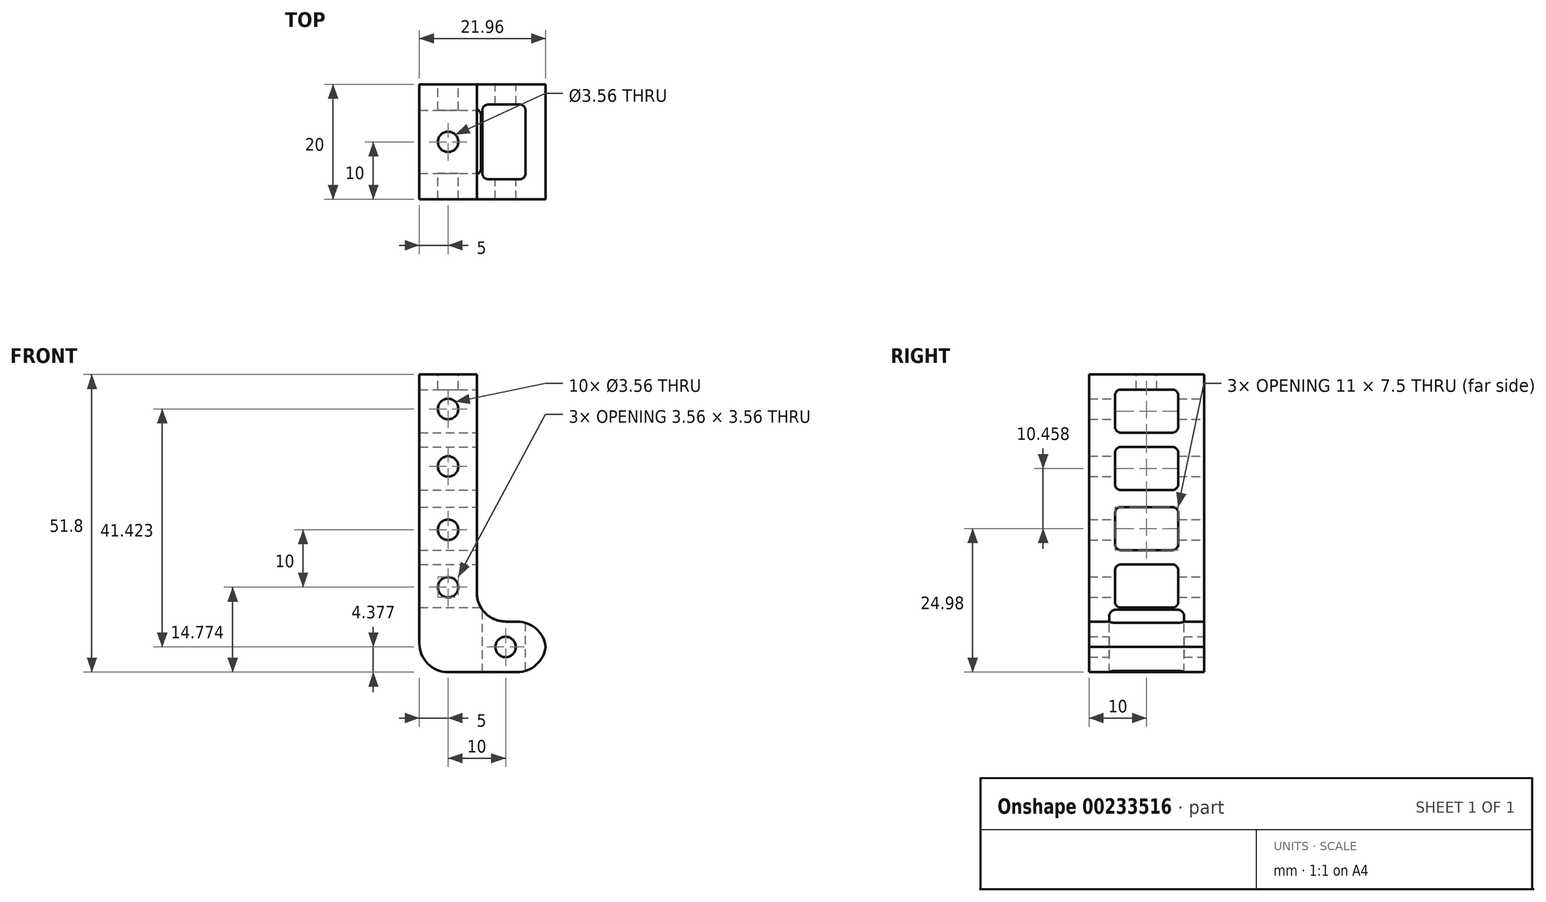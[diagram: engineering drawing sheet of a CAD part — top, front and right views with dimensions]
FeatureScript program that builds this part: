
annotation { "Feature Type Name" : "Feature", "Feature Type Description" : "" }
export const myFeature = defineFeature(function(context is Context, id is Id, definition is map)
    precondition{}
    {
        {
            var Q0;
            Q0=qCreatedBy(makeId("Front.planeOp"),FACE);
            var sketch = newSketch(context, id + "F0", { "sketchPlane" : qUnion([Q0])});
            skLineSegment(sketch, "E0.top", {"start": v(0, 43) * mm, "end": v(10, 43) * mm});
            skLineSegment(sketch, "E0.left", {"start": v(0, 0) * mm, "end": v(0, 43) * mm});
            skLineSegment(sketch, "E0.right", {"start": v(10, 5) * mm, "end": v(10, 43) * mm});
            skCircle(sketch, "E1", {"center": v(5, 15.97) * mm, "radius": 1.78 * mm});
            skCircle(sketch, "E2", {"center": v(5, 5.97) * mm, "radius": 1.78 * mm});
            skCircle(sketch, "E3", {"center": v(15, -4.42) * mm, "radius": 1.78 * mm});
            skLineSegment(sketch, "E4.bottom", {"start": v(15, 0) * mm, "end": v(17, 0) * mm});
            skLineSegment(sketch, "E4.top", {"start": v(5, -8.8) * mm, "end": v(17, -8.8) * mm});
            skLineSegment(sketch, "E4.left", {"start": v(0, 0) * mm, "end": v(0, -3.8) * mm});
            skLineSegment(sketch, "E4.right", {"start": v(22, -3.8) * mm, "end": v(22, -5) * mm});
            skPoint(sketch, "E5.visualSharp", {"position": v(10, 0) * mm});
            skArc(sketch, "E5.filletArc", {"start": v(10, 5) * mm, "mid": v(11.46, 1.46) * mm, "end": v(15, 0) * mm});
            skPoint(sketch, "E6.visualSharp", {"position": v(0, -8.8) * mm});
            skArc(sketch, "E6.filletArc", {"start": v(0, -3.8) * mm, "mid": v(1.46, -7.33) * mm, "end": v(5, -8.8) * mm});
            skPoint(sketch, "E7.visualSharp", {"position": v(22, -8.8) * mm});
            skArc(sketch, "E7.filletArc", {"start": v(17, -8.8) * mm, "mid": v(20.54, -7.33) * mm, "end": v(22, -3.8) * mm});
            skPoint(sketch, "E8.visualSharp", {"position": v(22, 0) * mm});
            skArc(sketch, "E8.filletArc", {"start": v(22, -5) * mm, "mid": v(20.54, -1.46) * mm, "end": v(17, 0) * mm});
            skCircle(sketch, "E9", {"center": v(5, 27) * mm, "radius": 1.78 * mm});
            skCircle(sketch, "E10.0.1.0", {"center": v(5, 37) * mm, "radius": 1.78 * mm});
            skLineSegment(sketch, "E10.direction1", {"start": v(5, 27) * mm, "end": v(30, 27) * mm, "construction": true});
            skLineSegment(sketch, "E10.direction2", {"start": v(5, 27) * mm, "end": v(5, 37) * mm, "construction": true});
            skSolve(sketch);
        }
        {
            var Q0;
            Q0 = qSketchRegion(id + "F0", true);
            extrude(context, id + "F1", {"entities" : qUnion([Q0]), "depth" : 20 * mm});
        }
        {
            var Q0;
            Q0=makeQuery(id+"F1.opExtrude","SWEPT_FACE",FACE,{"disambiguationData":[OSD([sQuery(id+"F0.wireOp",EDGE,"E0.right")])]});
            var sketch = newSketch(context, id + "F2", { "sketchPlane" : qUnion([Q0])});
            skLineSegment(sketch, "E11.bottom", {"start": v(-14.5, 2.43) * mm, "end": v(-5.5, 2.43) * mm});
            skLineSegment(sketch, "E11.top", {"start": v(-14.5, 9.93) * mm, "end": v(-5.5, 9.93) * mm});
            skLineSegment(sketch, "E12", {"start": v(-15.5, 3.43) * mm, "end": v(-15.5, 8.93) * mm});
            skLineSegment(sketch, "E13", {"start": v(-4.5, 3.43) * mm, "end": v(-4.5, 8.93) * mm});
            skPoint(sketch, "E14.visualSharp", {"position": v(-15.5, 9.93) * mm});
            skArc(sketch, "E14.filletArc", {"start": v(-14.5, 9.93) * mm, "mid": v(-15.2, 9.64) * mm, "end": v(-15.5, 8.93) * mm});
            skPoint(sketch, "E15.visualSharp", {"position": v(-15.5, 2.43) * mm});
            skArc(sketch, "E15.filletArc", {"start": v(-15.5, 3.43) * mm, "mid": v(-15.2, 2.72) * mm, "end": v(-14.5, 2.43) * mm});
            skPoint(sketch, "E16.visualSharp", {"position": v(-4.5, 2.43) * mm});
            skArc(sketch, "E16.filletArc", {"start": v(-5.5, 2.43) * mm, "mid": v(-4.8, 2.72) * mm, "end": v(-4.5, 3.43) * mm});
            skPoint(sketch, "E17.visualSharp", {"position": v(-4.5, 9.93) * mm});
            skArc(sketch, "E17.filletArc", {"start": v(-4.5, 8.93) * mm, "mid": v(-4.8, 9.64) * mm, "end": v(-5.5, 9.93) * mm});
            skPoint(sketch, "E18.0.1.0", {"position": v(-4.5, 19.93) * mm});
            skPoint(sketch, "E18.0.1.1", {"position": v(-4.5, 12.43) * mm});
            skPoint(sketch, "E18.0.1.2", {"position": v(-15.5, 12.43) * mm});
            skLineSegment(sketch, "E18.0.1.3", {"start": v(-14.5, 19.93) * mm, "end": v(-5.5, 19.93) * mm});
            skLineSegment(sketch, "E18.0.1.4", {"start": v(-14.5, 12.43) * mm, "end": v(-5.5, 12.43) * mm});
            skPoint(sketch, "E18.0.1.5", {"position": v(-15.5, 19.93) * mm});
            skArc(sketch, "E18.0.1.6", {"start": v(-14.5, 19.93) * mm, "mid": v(-15.2, 19.64) * mm, "end": v(-15.5, 18.93) * mm});
            skArc(sketch, "E18.0.1.7", {"start": v(-15.5, 13.43) * mm, "mid": v(-15.2, 12.72) * mm, "end": v(-14.5, 12.43) * mm});
            skArc(sketch, "E18.0.1.8", {"start": v(-4.5, 18.93) * mm, "mid": v(-4.8, 19.64) * mm, "end": v(-5.5, 19.93) * mm});
            skArc(sketch, "E18.0.1.9", {"start": v(-5.5, 12.43) * mm, "mid": v(-4.8, 12.72) * mm, "end": v(-4.5, 13.43) * mm});
            skLineSegment(sketch, "E18.0.1.10", {"start": v(-4.5, 13.43) * mm, "end": v(-4.5, 18.93) * mm});
            skLineSegment(sketch, "E18.0.1.11", {"start": v(-15.5, 13.43) * mm, "end": v(-15.5, 18.93) * mm});
            skLineSegment(sketch, "E18.direction1", {"start": v(-15.5, 2.43) * mm, "end": v(9.5, 2.43) * mm, "construction": true});
            skLineSegment(sketch, "E18.direction2", {"start": v(-15.5, 2.43) * mm, "end": v(-15.5, 12.43) * mm, "construction": true});
            skLineSegment(sketch, "E19", {"start": v(-20, 21.4) * mm, "end": v(-10.8, 21.4) * mm, "construction": true});
            skArc(sketch, "E20.MirrorCS", {"start": v(-15.5, 39.39) * mm, "mid": v(-15.2, 40.1) * mm, "end": v(-14.5, 40.39) * mm});
            skArc(sketch, "E21.MirrorCS", {"start": v(-15.5, 29.39) * mm, "mid": v(-15.2, 30.1) * mm, "end": v(-14.5, 30.39) * mm});
            skArc(sketch, "E22.MirrorCS", {"start": v(-14.5, 22.89) * mm, "mid": v(-15.2, 23.18) * mm, "end": v(-15.5, 23.89) * mm});
            skArc(sketch, "E23.MirrorCS", {"start": v(-14.5, 32.89) * mm, "mid": v(-15.2, 33.18) * mm, "end": v(-15.5, 33.89) * mm});
            skArc(sketch, "E24.MirrorCS", {"start": v(-4.5, 23.89) * mm, "mid": v(-4.8, 23.18) * mm, "end": v(-5.5, 22.89) * mm});
            skArc(sketch, "E25.MirrorCS", {"start": v(-5.5, 30.39) * mm, "mid": v(-4.8, 30.1) * mm, "end": v(-4.5, 29.39) * mm});
            skLineSegment(sketch, "E26.MirrorCS", {"start": v(-15.5, 39.39) * mm, "end": v(-15.5, 33.89) * mm});
            skArc(sketch, "E27.MirrorCS", {"start": v(-5.5, 40.39) * mm, "mid": v(-4.8, 40.1) * mm, "end": v(-4.5, 39.39) * mm});
            skArc(sketch, "E28.MirrorCS", {"start": v(-4.5, 33.89) * mm, "mid": v(-4.8, 33.18) * mm, "end": v(-5.5, 32.89) * mm});
            skLineSegment(sketch, "E29.MirrorCS", {"start": v(-14.5, 22.89) * mm, "end": v(-5.5, 22.89) * mm});
            skPoint(sketch, "E30.MirrorP", {"position": v(-4.5, 30.39) * mm});
            skLineSegment(sketch, "E31.MirrorCS", {"start": v(-15.5, 29.39) * mm, "end": v(-15.5, 23.89) * mm});
            skLineSegment(sketch, "E32.MirrorCS", {"start": v(-15.5, 40.39) * mm, "end": v(-15.5, 30.39) * mm, "construction": true});
            skLineSegment(sketch, "E33.MirrorCS", {"start": v(-14.5, 30.39) * mm, "end": v(-5.5, 30.39) * mm});
            skLineSegment(sketch, "E34.MirrorCS", {"start": v(-14.5, 32.89) * mm, "end": v(-5.5, 32.89) * mm});
            skPoint(sketch, "E35.MirrorP", {"position": v(-4.5, 32.89) * mm});
            skPoint(sketch, "E36.MirrorP", {"position": v(-15.5, 22.89) * mm});
            skLineSegment(sketch, "E37.MirrorCS", {"start": v(-4.5, 39.39) * mm, "end": v(-4.5, 33.89) * mm});
            skPoint(sketch, "E38.MirrorP", {"position": v(-15.5, 32.89) * mm});
            skPoint(sketch, "E39.MirrorP", {"position": v(-15.5, 30.39) * mm});
            skLineSegment(sketch, "E40.MirrorCS", {"start": v(-4.5, 29.39) * mm, "end": v(-4.5, 23.89) * mm});
            skPoint(sketch, "E41.MirrorP", {"position": v(-15.5, 40.39) * mm});
            skPoint(sketch, "E42.MirrorP", {"position": v(-4.5, 40.39) * mm});
            skPoint(sketch, "E43.MirrorP", {"position": v(-4.5, 22.89) * mm});
            skLineSegment(sketch, "E44.MirrorCS", {"start": v(-14.5, 40.39) * mm, "end": v(-5.5, 40.39) * mm});
            skSolve(sketch);
        }
        {
            var Q0;
            Q0 = qSketchRegion(id + "F2", true);
            extrude(context, id + "F3", {"entities" : qUnion([Q0]), "operationType" : NewBodyOperationType.REMOVE, "oppositeDirection" : true, "depth" : 25 * mm, "hasSecondDirection" : true, "secondDirectionOppositeDirection" : false, "secondDirectionDepth" : 25 * mm});
        }
        {
            var Q0;
            Q0=makeQuery(id+"F1.opExtrude","SWEPT_FACE",FACE,{"disambiguationData":[OSD([sQuery(id+"F0.wireOp",EDGE,"E4.bottom")])]});
            var sketch = newSketch(context, id + "F4", { "sketchPlane" : qUnion([Q0])});
            skLineSegment(sketch, "E45.bottom", {"start": v(17.46, -16.5) * mm, "end": v(11.96, -16.5) * mm});
            skLineSegment(sketch, "E45.top", {"start": v(17.46, -3.5) * mm, "end": v(11.96, -3.5) * mm});
            skLineSegment(sketch, "E45.left", {"start": v(18.46, -15.5) * mm, "end": v(18.46, -4.5) * mm});
            skLineSegment(sketch, "E45.right", {"start": v(10.96, -15.5) * mm, "end": v(10.96, -4.5) * mm});
            skPoint(sketch, "E46.visualSharp", {"position": v(10.96, -16.5) * mm});
            skArc(sketch, "E46.filletArc", {"start": v(10.96, -15.5) * mm, "mid": v(11.26, -16.2) * mm, "end": v(11.96, -16.5) * mm});
            skPoint(sketch, "E47.visualSharp", {"position": v(10.96, -3.5) * mm});
            skArc(sketch, "E47.filletArc", {"start": v(11.96, -3.5) * mm, "mid": v(11.26, -3.8) * mm, "end": v(10.96, -4.5) * mm});
            skPoint(sketch, "E48.visualSharp", {"position": v(18.46, -3.5) * mm});
            skArc(sketch, "E48.filletArc", {"start": v(18.46, -4.5) * mm, "mid": v(18.17, -3.8) * mm, "end": v(17.46, -3.5) * mm});
            skPoint(sketch, "E49.visualSharp", {"position": v(18.46, -16.5) * mm});
            skArc(sketch, "E49.filletArc", {"start": v(17.46, -16.5) * mm, "mid": v(18.17, -16.2) * mm, "end": v(18.46, -15.5) * mm});
            skSolve(sketch);
        }
        {
            var Q0;
            Q0 = qSketchRegion(id + "F4", true);
            extrude(context, id + "F5", {"entities" : qUnion([Q0]), "operationType" : NewBodyOperationType.REMOVE, "oppositeDirection" : true, "depth" : 25 * mm, "hasSecondDirection" : true, "secondDirectionOppositeDirection" : false, "secondDirectionDepth" : 25 * mm});
        }
        {
            var Q0;
            Q0=makeQuery(id+"F1.opExtrude","SWEPT_FACE",FACE,{"disambiguationData":[OSD([sQuery(id+"F0.wireOp",EDGE,"E0.top")])]});
            var sketch = newSketch(context, id + "F6", { "sketchPlane" : qUnion([Q0])});
            skCircle(sketch, "E50", {"center": v(5, -13.5) * mm, "radius": 1.78 * mm});
            skPoint(sketch, "E50.centerSnap0", {"position": v(5, -20) * mm});
            skLineSegment(sketch, "E51", {"start": v(0, -10) * mm, "end": v(10, -10) * mm, "construction": true});
            skCircle(sketch, "E52.MirrorC", {"center": v(5, -6.5) * mm, "radius": 1.78 * mm});
            skSolve(sketch);
        }
        {
            var Q0;
            Q0 = qSketchRegion(id + "F6", true);
            extrude(context, id + "F7", {"entities" : qUnion([Q0]), "operationType" : NewBodyOperationType.ADD, "endBound" : BoundingType.UP_TO_NEXT, "oppositeDirection" : true, "depth" : 25 * mm});
        }
        {
            var Q0;
            Q0=makeQuery(id+"F1.opExtrude","SWEPT_FACE",FACE,{"disambiguationData":[OSD([sQuery(id+"F0.wireOp",EDGE,"E0.top")])]});
            var sketch = newSketch(context, id + "F8", { "sketchPlane" : qUnion([Q0])});
            skCircle(sketch, "E53", {"center": v(5, -10) * mm, "radius": 1.78 * mm});
            skPoint(sketch, "E53.centerSnap0", {"position": v(10, -10) * mm});
            skSolve(sketch);
        }
        {
            var Q0;
            Q0 = qSketchRegion(id + "F8", true);
            extrude(context, id + "F9", {"entities" : qUnion([Q0]), "operationType" : NewBodyOperationType.REMOVE, "oppositeDirection" : true, "depth" : 5 * mm});
        }
        {
            var Q0;
            Q0=makeQuery(id+"F1.opExtrude","SWEPT_BODY",BODY,{"disambiguationData":[OSD([sQuery(id+"F0.wireOp",EDGE,"E4.right"),sQuery(id+"F0.wireOp",EDGE,"E7.filletArc"),sQuery(id+"F0.wireOp",EDGE,"E8.filletArc")])]});
            deleteBodies(context, id + "F10", {"entities" : qUnion([Q0])});
        }
    });
